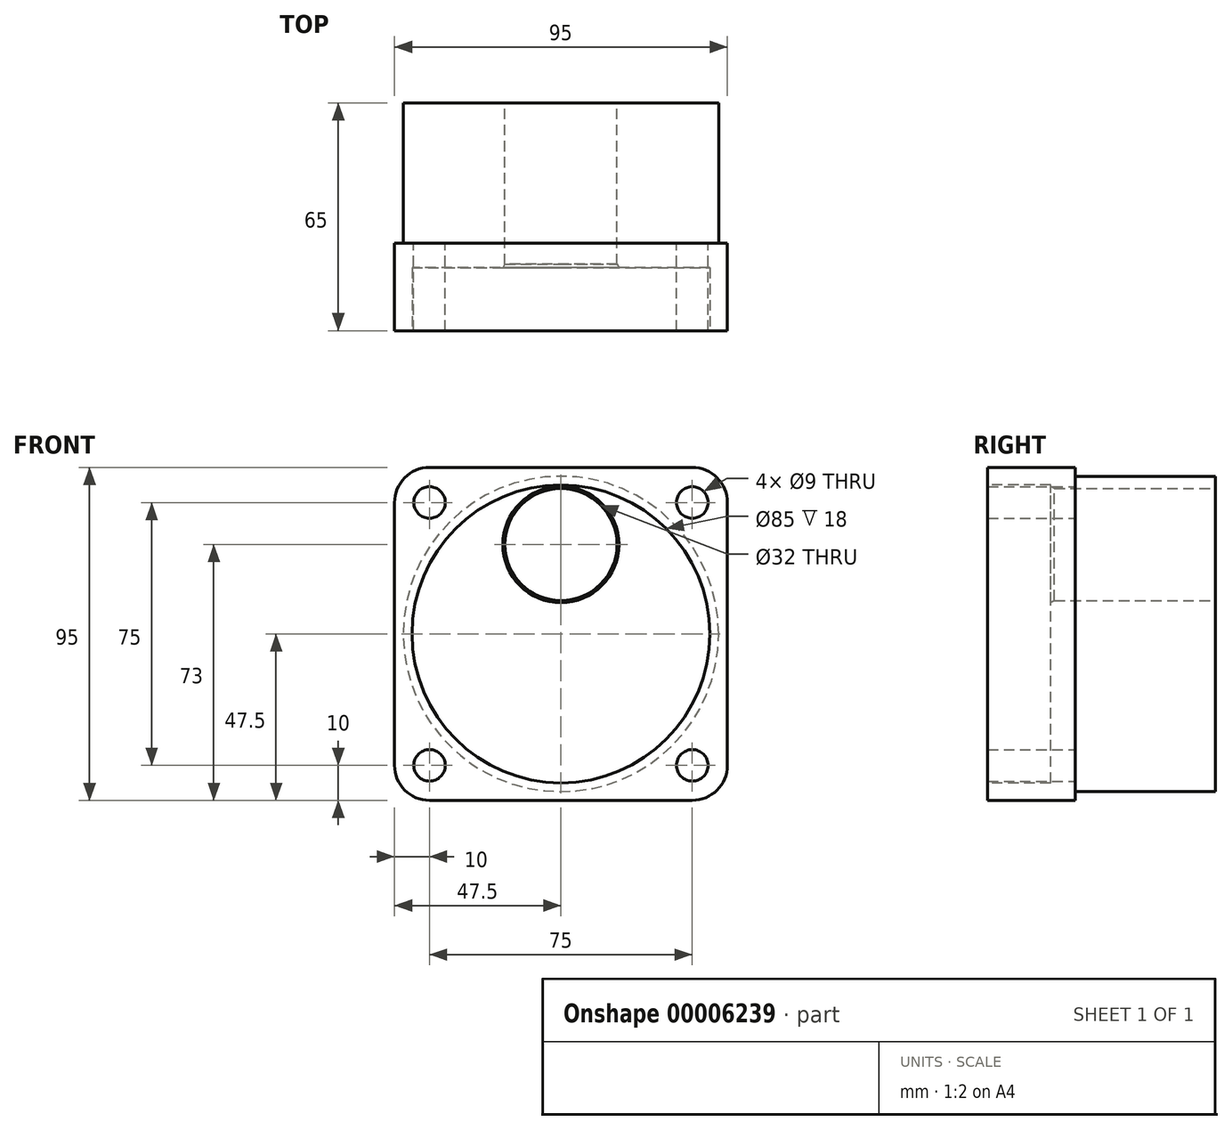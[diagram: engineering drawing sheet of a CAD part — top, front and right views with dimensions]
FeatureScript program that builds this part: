
annotation { "Feature Type Name" : "Feature", "Feature Type Description" : "" }
export const myFeature = defineFeature(function(context is Context, id is Id, definition is map)
    precondition{}
    {
        {
            var Q0;
            Q0=qCreatedBy(makeId("Front.planeOp"),FACE);
            var sketch = newSketch(context, id + "F0", { "sketchPlane" : qUnion([Q0])});
            skCircle(sketch, "E0", {"center": v(0, 0) * mm, "radius": 45 * mm});
            skSolve(sketch);
        }
        {
            var Q0;
            Q0=makeQuery(id+"F0.imprint","IMPRINT",FACE,{"disambiguationData":[TD([[makeQuery(id+"F0.imprint","IMPRINT",EDGE,{"derivedFrom":sQuery(id+"F0.wireOp",EDGE,"E0")}),1.0]])]});
            extrude(context, id + "F1", {"entities" : qUnion([Q0]), "oppositeDirection" : true, "depth" : 40 * mm, "offsetDistance" : 25 * mm});
        }
        {
            var Q0;
            Q0=qCreatedBy(makeId("Right.planeOp"),FACE);
            var sketch = newSketch(context, id + "F2", { "sketchPlane" : qUnion([Q0])});
            skLineSegment(sketch, "E1", {"start": v(-26.16, 0) * mm, "end": v(48.48, 0) * mm, "construction": true});
            skSolve(sketch);
        }
        {
            var Q0;
            Q0=makeQuery(id+"F0.imprint","IMPRINT",FACE,{"disambiguationData":[TD([[makeQuery(id+"F0.imprint","IMPRINT",EDGE,{"derivedFrom":sQuery(id+"F0.wireOp",EDGE,"E0")}),1.0]])]});
            var sketch = newSketch(context, id + "F3", { "sketchPlane" : qUnion([Q0])});
            skLineSegment(sketch, "E2.bottom", {"start": v(-37.5, 47.5) * mm, "end": v(37.5, 47.5) * mm});
            skLineSegment(sketch, "E2.top", {"start": v(-37.5, -47.5) * mm, "end": v(37.5, -47.5) * mm});
            skLineSegment(sketch, "E2.left", {"start": v(-47.5, 37.5) * mm, "end": v(-47.5, -37.5) * mm});
            skLineSegment(sketch, "E2.right", {"start": v(47.5, 37.5) * mm, "end": v(47.5, -37.5) * mm});
            skPoint(sketch, "E2.middle", {"position": v(0, 0) * mm});
            skPoint(sketch, "E3.visualSharp", {"position": v(-47.5, 47.5) * mm});
            skArc(sketch, "E3.filletArc", {"start": v(-37.5, 47.5) * mm, "mid": v(-44.57, 44.57) * mm, "end": v(-47.5, 37.5) * mm});
            skPoint(sketch, "E4.visualSharp", {"position": v(47.5, 47.5) * mm});
            skArc(sketch, "E4.filletArc", {"start": v(47.5, 37.5) * mm, "mid": v(44.57, 44.57) * mm, "end": v(37.5, 47.5) * mm});
            skPoint(sketch, "E5.visualSharp", {"position": v(47.5, -47.5) * mm});
            skArc(sketch, "E5.filletArc", {"start": v(37.5, -47.5) * mm, "mid": v(44.57, -44.57) * mm, "end": v(47.5, -37.5) * mm});
            skPoint(sketch, "E6.visualSharp", {"position": v(-47.5, -47.5) * mm});
            skArc(sketch, "E6.filletArc", {"start": v(-47.5, -37.5) * mm, "mid": v(-44.57, -44.57) * mm, "end": v(-37.5, -47.5) * mm});
            skSolve(sketch);
        }
        {
            var Q0;
            Q0=makeQuery(id+"F3.imprint","IMPRINT",FACE,{"disambiguationData":[TD([[makeQuery(id+"F3.imprint","IMPRINT",EDGE,{"derivedFrom":sQuery(id+"F3.wireOp",EDGE,"E2.bottom")}),-1.0]])]});
            var Q1;
            Q1=makeQuery(id+"F0.imprint","IMPRINT",FACE,{"disambiguationData":[TD([[makeQuery(id+"F0.imprint","IMPRINT",EDGE,{"derivedFrom":sQuery(id+"F0.wireOp",EDGE,"E0")}),1.0]])]});
            extrude(context, id + "F4", {"entities" : qUnion([Q0, Q1]), "operationType" : NewBodyOperationType.ADD, "depth" : 25 * mm});
        }
        {
            var Q0;
            {var subQ0=sQuery(id+"F0.wireOp",EDGE,"E0");Q0=makeQuery(id+"F4.boolean.opBoolean","MERGE",FACE,{"derivedFrom":[makeQuery(id+"F4.opExtrude","CAP_FACE",FACE,{"disambiguationData":[OSD([subQ0])],"isStart":false}),makeQuery(id+"F4.opExtrude","CAP_FACE",FACE,{"disambiguationData":[OSD([subQ0,sQuery(id+"F3.wireOp",EDGE,"E2.bottom"),sQuery(id+"F3.wireOp",EDGE,"E2.top"),sQuery(id+"F3.wireOp",EDGE,"E2.left"),sQuery(id+"F3.wireOp",EDGE,"E2.right"),sQuery(id+"F3.wireOp",EDGE,"E3.filletArc"),sQuery(id+"F3.wireOp",EDGE,"E4.filletArc"),sQuery(id+"F3.wireOp",EDGE,"E5.filletArc"),sQuery(id+"F3.wireOp",EDGE,"E6.filletArc")])],"isStart":false})]});}
            var sketch = newSketch(context, id + "F5", { "sketchPlane" : qUnion([Q0])});
            skCircle(sketch, "E7", {"center": v(0, 0) * mm, "radius": 42.5 * mm});
            skSolve(sketch);
        }
        {
            var Q0;
            Q0=makeQuery(id+"F5.imprint","IMPRINT",FACE,{"disambiguationData":[TD([[makeQuery(id+"F5.imprint","IMPRINT",EDGE,{"derivedFrom":sQuery(id+"F5.wireOp",EDGE,"E7")}),1.0]])]});
            extrude(context, id + "F6", {"entities" : qUnion([Q0]), "operationType" : NewBodyOperationType.REMOVE, "oppositeDirection" : true, "depth" : 18 * mm});
        }
        {
            var Q0;
            {var subQ0=sQuery(id+"F0.wireOp",EDGE,"E0");Q0=makeQuery(id+"F4.boolean.opBoolean","MERGE",FACE,{"derivedFrom":[makeQuery(id+"F4.opExtrude","CAP_FACE",FACE,{"disambiguationData":[OSD([subQ0])],"isStart":false}),makeQuery(id+"F4.opExtrude","CAP_FACE",FACE,{"disambiguationData":[OSD([subQ0,sQuery(id+"F3.wireOp",EDGE,"E2.bottom"),sQuery(id+"F3.wireOp",EDGE,"E2.top"),sQuery(id+"F3.wireOp",EDGE,"E2.left"),sQuery(id+"F3.wireOp",EDGE,"E2.right"),sQuery(id+"F3.wireOp",EDGE,"E3.filletArc"),sQuery(id+"F3.wireOp",EDGE,"E4.filletArc"),sQuery(id+"F3.wireOp",EDGE,"E5.filletArc"),sQuery(id+"F3.wireOp",EDGE,"E6.filletArc")])],"isStart":false})]});}
            var sketch = newSketch(context, id + "F7", { "sketchPlane" : qUnion([Q0])});
            skPoint(sketch, "E8", {"position": v(-37.5, 37.5) * mm});
            skPoint(sketch, "E9", {"position": v(37.5, 37.5) * mm});
            skPoint(sketch, "E10", {"position": v(37.5, -37.5) * mm});
            skPoint(sketch, "E11", {"position": v(-42.08, -46.39) * mm});
            skPoint(sketch, "E12", {"position": v(-37.5, -37.5) * mm});
            skSolve(sketch);
        }
        {
            var Q0;
            Q0=sQuery(id+"F7.wireOp",VERTEX,"E8");
            var Q1;
            Q1=sQuery(id+"F7.wireOp",VERTEX,"E9");
            var Q2;
            Q2=sQuery(id+"F7.wireOp",VERTEX,"E10");
            var Q3;
            Q3=sQuery(id+"F7.wireOp",VERTEX,"E12");
            var Q4;
            Q4=makeQuery(id+"F1.opExtrude","SWEPT_BODY",BODY,{"disambiguationData":[OSD([sQuery(id+"F0.wireOp",EDGE,"E0")])]});
            hole(context, id + "F8", {"style" : HoleStyle.SIMPLE, "endStyle" : HoleEndStyle.THROUGH, "holeDiameter" : 9 * mm, "locations" : qUnion([Q0, Q1, Q2, Q3]), "scope" : qUnion([Q4]), "isTappedThrough" : true});
        }
        {
            var Q0;
            Q0=qCreatedBy(makeId("Right.planeOp"),FACE);
            var sketch = newSketch(context, id + "F9", { "sketchPlane" : qUnion([Q0])});
            skLineSegment(sketch, "E13", {"start": v(-9.84, 25.5) * mm, "end": v(57.92, 25.5) * mm, "construction": true});
            skLineSegment(sketch, "E14.bottom", {"start": v(-8.3, 25.5) * mm, "end": v(42.87, 25.5) * mm});
            skLineSegment(sketch, "E14.top", {"start": v(-8.3, 9.5) * mm, "end": v(42.87, 9.5) * mm});
            skLineSegment(sketch, "E14.left", {"start": v(-8.3, 25.5) * mm, "end": v(-8.3, 9.5) * mm});
            skLineSegment(sketch, "E14.right", {"start": v(42.87, 25.5) * mm, "end": v(42.87, 9.5) * mm});
            skLineSegment(sketch, "E15.bottom", {"start": v(22, 9.5) * mm, "end": v(28, 9.5) * mm});
            skLineSegment(sketch, "E15.top", {"start": v(22, 7.5) * mm, "end": v(28, 7.5) * mm});
            skLineSegment(sketch, "E15.left", {"start": v(22, 9.5) * mm, "end": v(22, 7.5) * mm});
            skLineSegment(sketch, "E15.right", {"start": v(28, 9.5) * mm, "end": v(28, 7.5) * mm});
            skSolve(sketch);
        }
        {
            var Q0;
            Q0=makeQuery(id+"F9.imprint","IMPRINT",FACE,{"disambiguationData":[TD([[makeQuery(id+"F9.imprint","IMPRINT",EDGE,{"derivedFrom":sQuery(id+"F9.wireOp",EDGE,"E14.bottom")}),-1.0]])]});
            var Q1;
            Q1=makeQuery(id+"F9.imprint","IMPRINT",FACE,{"disambiguationData":[TD([[makeQuery(id+"F9.imprint","IMPRINT",EDGE,{"derivedFrom":sQuery(id+"F9.wireOp",EDGE,"E15.bottom")}),-1.0]])]});
            var Q2;
            Q2=sQuery(id+"F9.wireOp",EDGE,"E13");
            revolve(context, id + "F10", {"operationType" : NewBodyOperationType.REMOVE, "entities" : qUnion([Q0, Q1]), "axis" : qUnion([Q2]), "revolveType" : RevolveType.FULL, "oppositeDirection" : true});
        }
        {
            var Q0;
            {var subQ0=sQuery(id+"F9.wireOp",EDGE,"E14.top");Q0=makeQuery(id+"F10.boolean.opBoolean","INTERSECT",EDGE,{"derivedFrom":[makeQuery(id+"F6.boolean.opBoolean","COPY",FACE,{"derivedFrom":makeQuery(id+"F6.opExtrude","CAP_FACE",FACE,{"disambiguationData":[OSD([sQuery(id+"F5.wireOp",EDGE,"E7")])],"isStart":false})}),makeQuery(id+"F10.opRevolve","SWEPT_FACE",FACE,{"disambiguationData":[OSD([subQ0]),TDD([makeQuery(id+"F9.imprint","IMPRINT",EDGE,{"disambiguationData":[TD([[makeQuery(id+"F9.imprint","INTERSECT",VERTEX,{"derivedFrom":[subQ0,sQuery(id+"F9.wireOp",EDGE,"E14.left")]}),-1.0]])],"derivedFrom":subQ0})])]})]});}
            chamfer(context, id + "F11", {"entities" : qUnion([Q0]), "chamferType" : ChamferType.OFFSET_ANGLE, "width" : 1 * mm, "oppositeDirection" : true, "angle" : 30 * degree, "tangentPropagation" : true});
        }
    });
